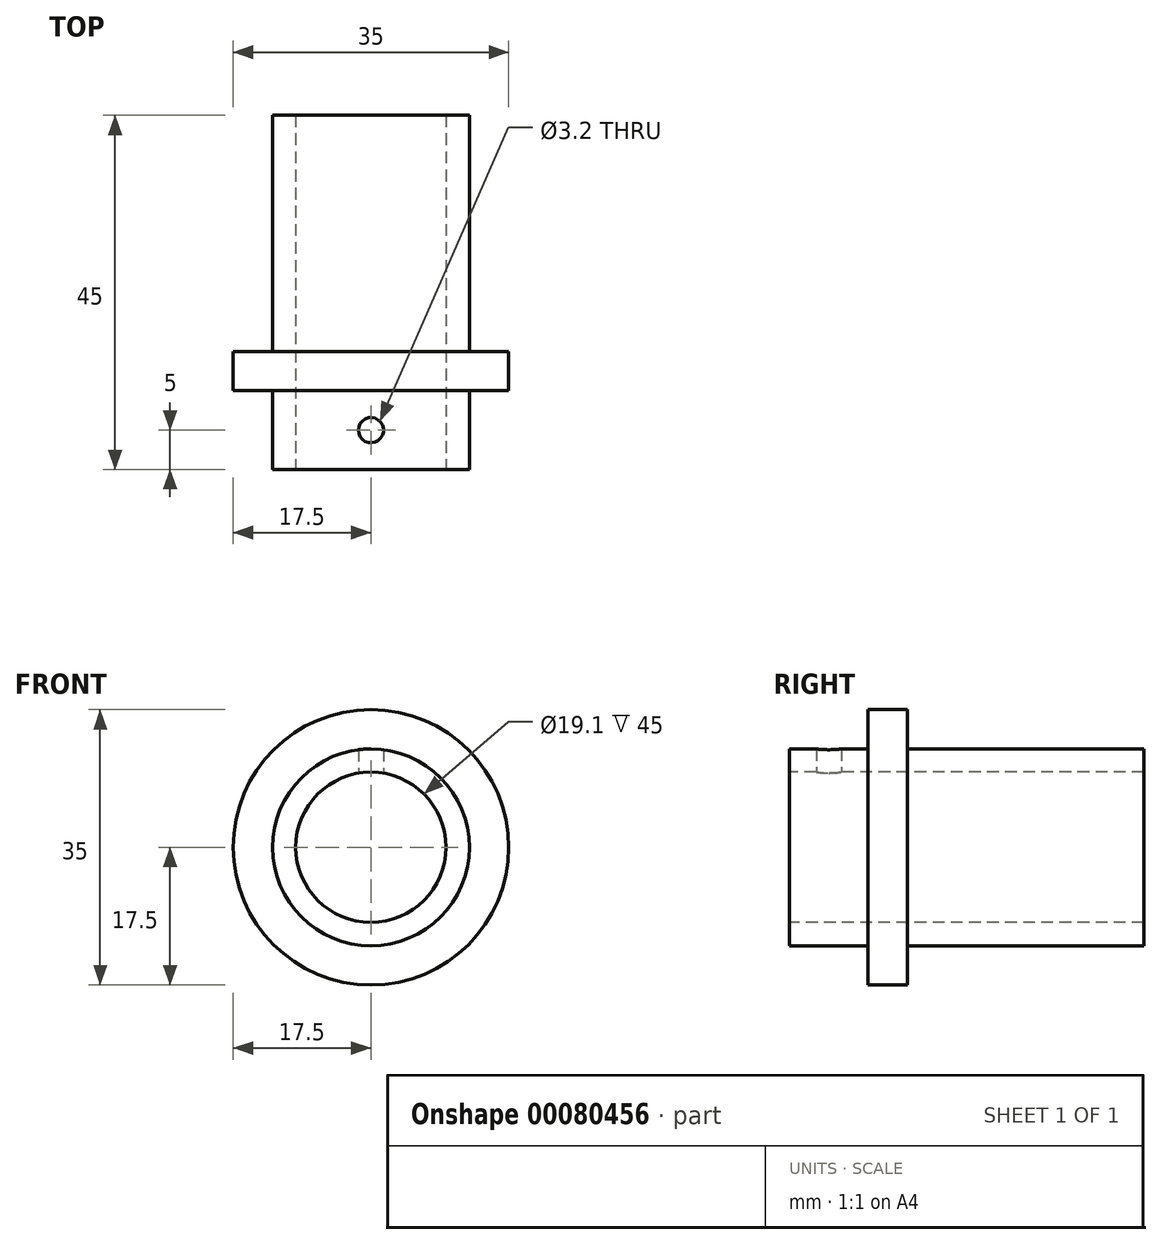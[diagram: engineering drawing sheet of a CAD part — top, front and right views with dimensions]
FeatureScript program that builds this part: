
annotation { "Feature Type Name" : "Feature", "Feature Type Description" : "" }
export const myFeature = defineFeature(function(context is Context, id is Id, definition is map)
    precondition{}
    {
        {
            var Q0;
            Q0=qCreatedBy(makeId("Right.planeOp"),FACE);
            var sketch = newSketch(context, id + "F0", { "sketchPlane" : qUnion([Q0])});
            skLineSegment(sketch, "E0", {"start": v(0, 0) * mm, "end": v(51.68, 0) * mm, "construction": true});
            skLineSegment(sketch, "E1", {"start": v(0, 9.55) * mm, "end": v(45, 9.55) * mm});
            skLineSegment(sketch, "E2", {"start": v(45, 9.55) * mm, "end": v(45, 12.5) * mm});
            skLineSegment(sketch, "E3", {"start": v(45, 12.5) * mm, "end": v(15, 12.5) * mm});
            skLineSegment(sketch, "E4", {"start": v(15, 12.5) * mm, "end": v(15, 17.5) * mm});
            skLineSegment(sketch, "E5", {"start": v(15, 17.5) * mm, "end": v(10, 17.5) * mm});
            skLineSegment(sketch, "E6", {"start": v(10, 17.5) * mm, "end": v(10, 12.5) * mm});
            skLineSegment(sketch, "E7", {"start": v(10, 12.5) * mm, "end": v(0, 12.5) * mm});
            skLineSegment(sketch, "E8", {"start": v(0, 12.5) * mm, "end": v(0, 9.55) * mm});
            skSolve(sketch);
        }
        {
            var Q0;
            Q0 = qSketchRegion(id + "F0", true);
            var Q1;
            Q1=sQuery(id+"F0.wireOp",EDGE,"E0");
            revolve(context, id + "F1", {"entities" : qUnion([Q0]), "axis" : qUnion([Q1]), "revolveType" : RevolveType.FULL});
        }
        {
            var Q0;
            Q0=qCreatedBy(makeId("Top.planeOp"),FACE);
            var sketch = newSketch(context, id + "F2", { "sketchPlane" : qUnion([Q0])});
            skCircle(sketch, "E9", {"center": v(0, 5) * mm, "radius": 1.6 * mm});
            skSolve(sketch);
        }
        {
            var Q0;
            Q0 = qSketchRegion(id + "F2", true);
            extrude(context, id + "F3", {"entities" : qUnion([Q0]), "operationType" : NewBodyOperationType.REMOVE, "endBound" : BoundingType.THROUGH_ALL, "depth" : 25 * mm});
        }
    });
